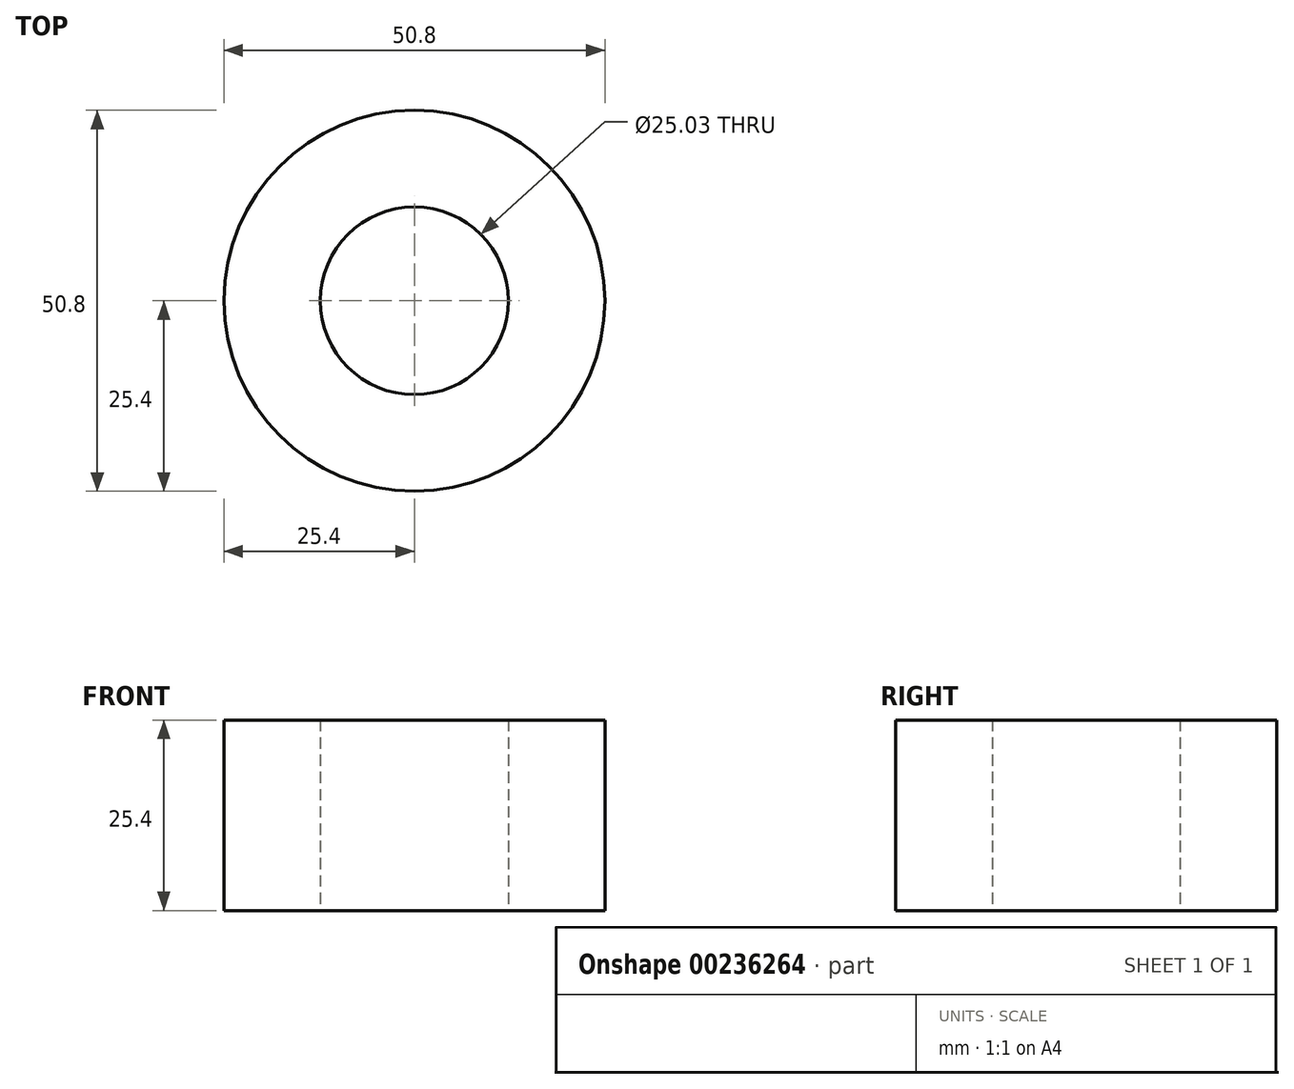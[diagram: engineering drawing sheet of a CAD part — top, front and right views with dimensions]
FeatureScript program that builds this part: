
annotation { "Feature Type Name" : "Feature", "Feature Type Description" : "" }
export const myFeature = defineFeature(function(context is Context, id is Id, definition is map)
    precondition{}
    {
        {
            var Q0;
            Q0=qCreatedBy(makeId("Top.planeOp"),FACE);
            var sketch = newSketch(context, id + "F0", { "sketchPlane" : qUnion([Q0])});
            skCircle(sketch, "E0", {"center": v(0, 0) * mm, "radius": 25.4 * mm});
            skCircle(sketch, "E1", {"center": v(0, 0) * mm, "radius": 12.52 * mm});
            skSolve(sketch);
        }
        {
            var Q0;
            Q0 = qSketchRegion(id + "F0", true);
            extrude(context, id + "F1", {"entities" : qUnion([Q0]), "depth" : 25.4 * mm});
        }
    });
